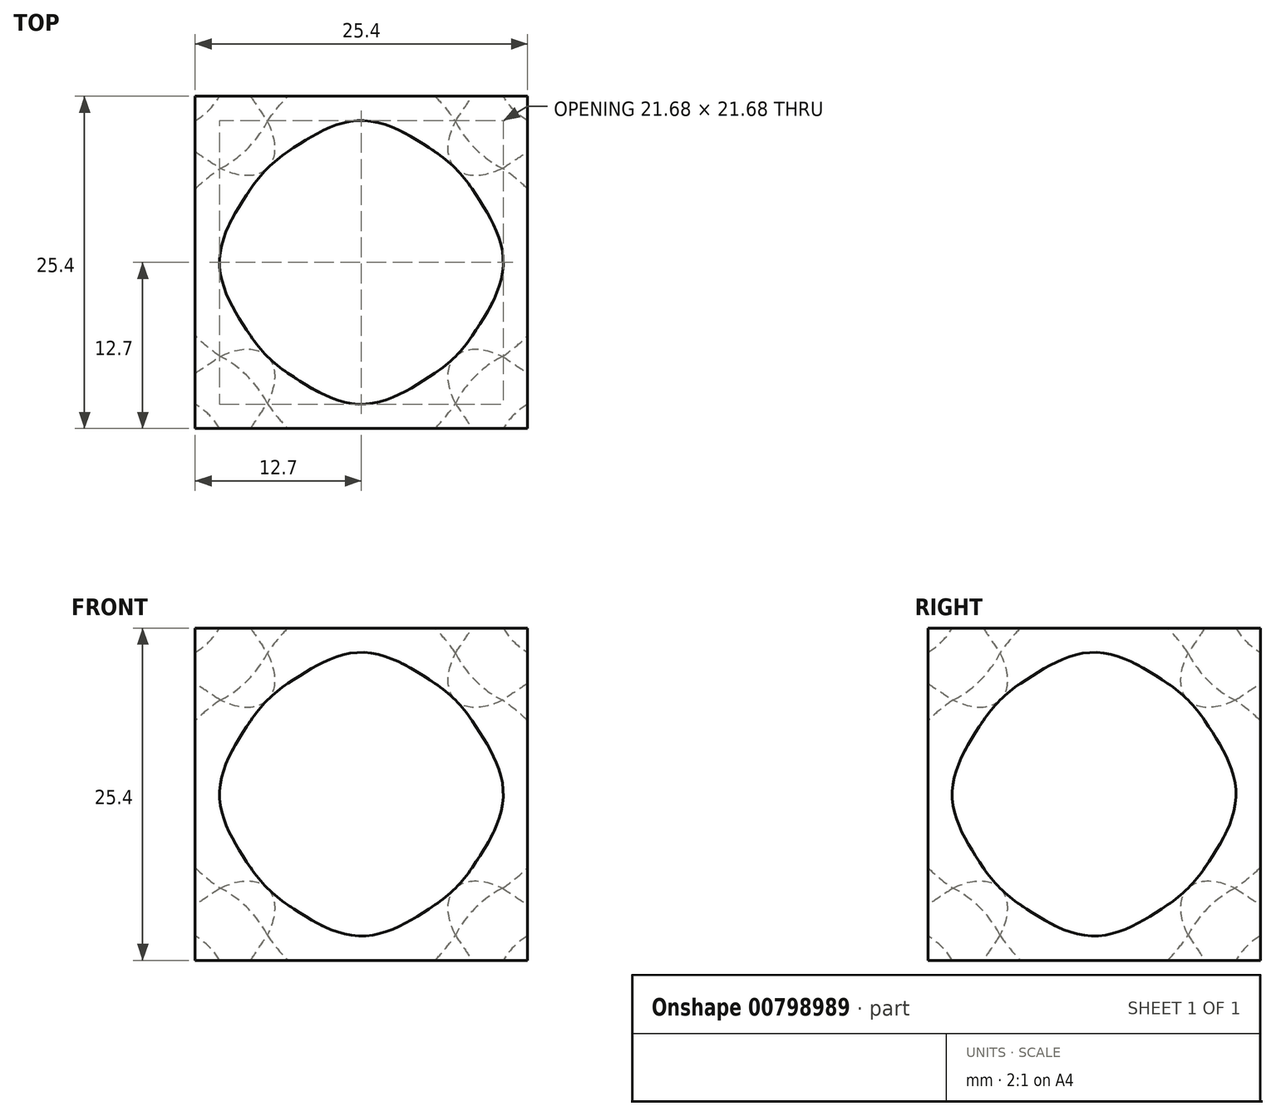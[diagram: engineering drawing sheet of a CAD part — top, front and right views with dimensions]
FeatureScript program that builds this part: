
annotation { "Feature Type Name" : "Feature", "Feature Type Description" : "" }
export const myFeature = defineFeature(function(context is Context, id is Id, definition is map)
    precondition{}
    {
        {
            var Q0;
            Q0=qCreatedBy(makeId("Top.planeOp"),FACE);
            var sketch = newSketch(context, id + "F0", { "sketchPlane" : qUnion([Q0])});
            skLineSegment(sketch, "E0.bottom", {"start": v(12.7, 12.7) * mm, "end": v(-12.7, 12.7) * mm});
            skLineSegment(sketch, "E0.top", {"start": v(12.7, -12.7) * mm, "end": v(-12.7, -12.7) * mm});
            skLineSegment(sketch, "E0.left", {"start": v(12.7, 12.7) * mm, "end": v(12.7, -12.7) * mm});
            skLineSegment(sketch, "E0.right", {"start": v(-12.7, 12.7) * mm, "end": v(-12.7, -12.7) * mm});
            skPoint(sketch, "E0.middle", {"position": v(0, 0) * mm});
            skCircle(sketch, "E1", {"center": v(0, 0) * mm, "radius": 10.16 * mm});
            skLineSegment(sketch, "E2", {"start": v(-12.7, 0) * mm, "end": v(12.7, 0) * mm});
            skLineSegment(sketch, "E3", {"start": v(0, 12.7) * mm, "end": v(0, -12.7) * mm});
            skSolve(sketch);
        }
        {
            var Q0;
            Q0 = qSketchRegion(id + "F0", true);
            extrude(context, id + "F1", {"entities" : qUnion([Q0]), "depth" : 25.4 * mm, "offsetDistance" : 25.4 * mm});
        }
        {
            var Q0;
            Q0=makeQuery(id+"F1.opExtrude","SWEPT_FACE",FACE,{"disambiguationData":[OSD([sQuery(id+"F0.wireOp",EDGE,"E0.bottom")])]});
            var sketch = newSketch(context, id + "F2", { "sketchPlane" : qUnion([Q0])});
            skLineSegment(sketch, "E4", {"start": v(12.7, 12.7) * mm, "end": v(-12.7, 12.7) * mm});
            skLineSegment(sketch, "E5", {"start": v(0, 25.4) * mm, "end": v(0, 0) * mm});
            skCircle(sketch, "E6", {"center": v(0, 12.7) * mm, "radius": 10.16 * mm});
            skSolve(sketch);
        }
        {
            var Q0;
            Q0 = qSketchRegion(id + "F2", true);
            extrude(context, id + "F3", {"entities" : qUnion([Q0]), "operationType" : NewBodyOperationType.REMOVE, "endBound" : BoundingType.THROUGH_ALL, "oppositeDirection" : true, "depth" : 25.4 * mm, "offsetDistance" : 25.4 * mm});
        }
        {
            var Q0;
            Q0=makeQuery(id+"F1.opExtrude","SWEPT_FACE",FACE,{"disambiguationData":[OSD([sQuery(id+"F0.wireOp",EDGE,"E0.right")])]});
            var sketch = newSketch(context, id + "F4", { "sketchPlane" : qUnion([Q0])});
            skLineSegment(sketch, "E7", {"start": v(0, 25.4) * mm, "end": v(0, 0) * mm});
            skLineSegment(sketch, "E8", {"start": v(12.7, 12.7) * mm, "end": v(-12.7, 12.7) * mm});
            skCircle(sketch, "E9", {"center": v(0, 12.7) * mm, "radius": 10.16 * mm});
            skSolve(sketch);
        }
        {
            var Q0;
            Q0 = qSketchRegion(id + "F4", true);
            extrude(context, id + "F5", {"entities" : qUnion([Q0]), "operationType" : NewBodyOperationType.REMOVE, "endBound" : BoundingType.THROUGH_ALL, "oppositeDirection" : true, "depth" : 25.4 * mm, "offsetDistance" : 25.4 * mm});
        }
        {
            var Q0;
            {var subQ0=sQuery(id+"F0.wireOp",EDGE,"E1");var subQ1=makeQuery(id+"F1.opExtrude","SWEPT_FACE",FACE,{"disambiguationData":[OSD([subQ0])]});Q0=makeQuery(id+"F5.boolean.opBoolean","INTERSECT",EDGE,{"disambiguationData":[OD(0.0)],"derivedFrom":[makeQuery(id+"F3.boolean.opBoolean","SPLIT",FACE,{"disambiguationData":[TD([makeQuery(id+"F1.opExtrude","CAP_FACE",FACE,{"disambiguationData":[OSD([sQuery(id+"F0.wireOp",EDGE,"E0.bottom"),sQuery(id+"F0.wireOp",EDGE,"E0.top"),sQuery(id+"F0.wireOp",EDGE,"E0.left"),sQuery(id+"F0.wireOp",EDGE,"E0.right"),subQ0])],"isStart":false})])],"derivedFrom":subQ1}),makeQuery(id+"F5.opExtrude","SWEPT_FACE",FACE,{"disambiguationData":[OSD([sQuery(id+"F4.wireOp",EDGE,"E9")])]})]});}
            var Q1;
            Q1=makeQuery(id+"F3.boolean.opBoolean","INTERSECT",EDGE,{"disambiguationData":[OD(2.0)],"derivedFrom":[makeQuery(id+"F1.opExtrude","SWEPT_FACE",FACE,{"disambiguationData":[OSD([sQuery(id+"F0.wireOp",EDGE,"E1")])]}),makeQuery(id+"F3.opExtrude","SWEPT_FACE",FACE,{"disambiguationData":[OSD([sQuery(id+"F2.wireOp",EDGE,"E6")])]})]});
            var Q2;
            Q2=makeQuery(id+"F3.boolean.opBoolean","INTERSECT",EDGE,{"disambiguationData":[OD(3.0)],"derivedFrom":[makeQuery(id+"F1.opExtrude","SWEPT_FACE",FACE,{"disambiguationData":[OSD([sQuery(id+"F0.wireOp",EDGE,"E1")])]}),makeQuery(id+"F3.opExtrude","SWEPT_FACE",FACE,{"disambiguationData":[OSD([sQuery(id+"F2.wireOp",EDGE,"E6")])]})]});
            var Q3;
            {var subQ0=sQuery(id+"F0.wireOp",EDGE,"E1");var subQ1=makeQuery(id+"F1.opExtrude","SWEPT_FACE",FACE,{"disambiguationData":[OSD([subQ0])]});Q3=makeQuery(id+"F5.boolean.opBoolean","INTERSECT",EDGE,{"disambiguationData":[OD(1.0)],"derivedFrom":[makeQuery(id+"F3.boolean.opBoolean","SPLIT",FACE,{"disambiguationData":[TD([makeQuery(id+"F1.opExtrude","CAP_FACE",FACE,{"disambiguationData":[OSD([sQuery(id+"F0.wireOp",EDGE,"E0.bottom"),sQuery(id+"F0.wireOp",EDGE,"E0.top"),sQuery(id+"F0.wireOp",EDGE,"E0.left"),sQuery(id+"F0.wireOp",EDGE,"E0.right"),subQ0])],"isStart":false})])],"derivedFrom":subQ1}),makeQuery(id+"F5.opExtrude","SWEPT_FACE",FACE,{"disambiguationData":[OSD([sQuery(id+"F4.wireOp",EDGE,"E9")])]})]});}
            var Q4;
            {var subQ0=makeQuery(id+"F3.opExtrude","SWEPT_FACE",FACE,{"disambiguationData":[OSD([sQuery(id+"F2.wireOp",EDGE,"E6")])]});Q4=makeQuery(id+"F5.boolean.opBoolean","INTERSECT",EDGE,{"disambiguationData":[OD(0.0)],"derivedFrom":[makeQuery(id+"F3.boolean.opBoolean","COPY",FACE,{"disambiguationData":[TD([makeQuery(id+"F1.opExtrude","SWEPT_FACE",FACE,{"disambiguationData":[OSD([sQuery(id+"F0.wireOp",EDGE,"E0.bottom")])]})])],"derivedFrom":subQ0}),makeQuery(id+"F5.opExtrude","SWEPT_FACE",FACE,{"disambiguationData":[OSD([sQuery(id+"F4.wireOp",EDGE,"E9")])]})]});}
            var Q5;
            {var subQ0=makeQuery(id+"F3.opExtrude","SWEPT_FACE",FACE,{"disambiguationData":[OSD([sQuery(id+"F2.wireOp",EDGE,"E6")])]});Q5=makeQuery(id+"F5.boolean.opBoolean","INTERSECT",EDGE,{"disambiguationData":[OD(0.0)],"derivedFrom":[makeQuery(id+"F3.boolean.opBoolean","COPY",FACE,{"disambiguationData":[TD([makeQuery(id+"F1.opExtrude","SWEPT_FACE",FACE,{"disambiguationData":[OSD([sQuery(id+"F0.wireOp",EDGE,"E0.top")])]})])],"derivedFrom":subQ0}),makeQuery(id+"F5.opExtrude","SWEPT_FACE",FACE,{"disambiguationData":[OSD([sQuery(id+"F4.wireOp",EDGE,"E9")])]})]});}
            var Q6;
            {var subQ0=sQuery(id+"F0.wireOp",EDGE,"E1");var subQ1=makeQuery(id+"F1.opExtrude","SWEPT_FACE",FACE,{"disambiguationData":[OSD([subQ0])]});Q6=makeQuery(id+"F5.boolean.opBoolean","INTERSECT",EDGE,{"disambiguationData":[OD(0.0)],"derivedFrom":[makeQuery(id+"F3.boolean.opBoolean","SPLIT",FACE,{"disambiguationData":[TD([makeQuery(id+"F1.opExtrude","CAP_FACE",FACE,{"disambiguationData":[OSD([sQuery(id+"F0.wireOp",EDGE,"E0.bottom"),sQuery(id+"F0.wireOp",EDGE,"E0.top"),sQuery(id+"F0.wireOp",EDGE,"E0.left"),sQuery(id+"F0.wireOp",EDGE,"E0.right"),subQ0])],"isStart":true})])],"derivedFrom":subQ1}),makeQuery(id+"F5.opExtrude","SWEPT_FACE",FACE,{"disambiguationData":[OSD([sQuery(id+"F4.wireOp",EDGE,"E9")])]})]});}
            var Q7;
            Q7=makeQuery(id+"F3.boolean.opBoolean","INTERSECT",EDGE,{"disambiguationData":[OD(1.0)],"derivedFrom":[makeQuery(id+"F1.opExtrude","SWEPT_FACE",FACE,{"disambiguationData":[OSD([sQuery(id+"F0.wireOp",EDGE,"E1")])]}),makeQuery(id+"F3.opExtrude","SWEPT_FACE",FACE,{"disambiguationData":[OSD([sQuery(id+"F2.wireOp",EDGE,"E6")])]})]});
            var Q8;
            {var subQ0=sQuery(id+"F0.wireOp",EDGE,"E1");var subQ1=makeQuery(id+"F1.opExtrude","SWEPT_FACE",FACE,{"disambiguationData":[OSD([subQ0])]});Q8=makeQuery(id+"F5.boolean.opBoolean","INTERSECT",EDGE,{"disambiguationData":[OD(1.0)],"derivedFrom":[makeQuery(id+"F3.boolean.opBoolean","SPLIT",FACE,{"disambiguationData":[TD([makeQuery(id+"F1.opExtrude","CAP_FACE",FACE,{"disambiguationData":[OSD([sQuery(id+"F0.wireOp",EDGE,"E0.bottom"),sQuery(id+"F0.wireOp",EDGE,"E0.top"),sQuery(id+"F0.wireOp",EDGE,"E0.left"),sQuery(id+"F0.wireOp",EDGE,"E0.right"),subQ0])],"isStart":true})])],"derivedFrom":subQ1}),makeQuery(id+"F5.opExtrude","SWEPT_FACE",FACE,{"disambiguationData":[OSD([sQuery(id+"F4.wireOp",EDGE,"E9")])]})]});}
            var Q9;
            Q9=makeQuery(id+"F3.boolean.opBoolean","INTERSECT",EDGE,{"disambiguationData":[OD(0.0)],"derivedFrom":[makeQuery(id+"F1.opExtrude","SWEPT_FACE",FACE,{"disambiguationData":[OSD([sQuery(id+"F0.wireOp",EDGE,"E1")])]}),makeQuery(id+"F3.opExtrude","SWEPT_FACE",FACE,{"disambiguationData":[OSD([sQuery(id+"F2.wireOp",EDGE,"E6")])]})]});
            var Q10;
            {var subQ0=makeQuery(id+"F3.opExtrude","SWEPT_FACE",FACE,{"disambiguationData":[OSD([sQuery(id+"F2.wireOp",EDGE,"E6")])]});Q10=makeQuery(id+"F5.boolean.opBoolean","INTERSECT",EDGE,{"disambiguationData":[OD(1.0)],"derivedFrom":[makeQuery(id+"F3.boolean.opBoolean","COPY",FACE,{"disambiguationData":[TD([makeQuery(id+"F1.opExtrude","SWEPT_FACE",FACE,{"disambiguationData":[OSD([sQuery(id+"F0.wireOp",EDGE,"E0.top")])]})])],"derivedFrom":subQ0}),makeQuery(id+"F5.opExtrude","SWEPT_FACE",FACE,{"disambiguationData":[OSD([sQuery(id+"F4.wireOp",EDGE,"E9")])]})]});}
            var Q11;
            {var subQ0=makeQuery(id+"F3.opExtrude","SWEPT_FACE",FACE,{"disambiguationData":[OSD([sQuery(id+"F2.wireOp",EDGE,"E6")])]});Q11=makeQuery(id+"F5.boolean.opBoolean","INTERSECT",EDGE,{"disambiguationData":[OD(1.0)],"derivedFrom":[makeQuery(id+"F3.boolean.opBoolean","COPY",FACE,{"disambiguationData":[TD([makeQuery(id+"F1.opExtrude","SWEPT_FACE",FACE,{"disambiguationData":[OSD([sQuery(id+"F0.wireOp",EDGE,"E0.bottom")])]})])],"derivedFrom":subQ0}),makeQuery(id+"F5.opExtrude","SWEPT_FACE",FACE,{"disambiguationData":[OSD([sQuery(id+"F4.wireOp",EDGE,"E9")])]})]});}
            fillet(context, id + "F6", {"entities" : qUnion([Q0, Q1, Q2, Q3, Q4, Q5, Q6, Q7, Q8, Q9, Q10, Q11]), "radius" : 5.08 * mm, "tangentPropagation" : true, "allowEdgeOverflow" : false});
        }
    });
